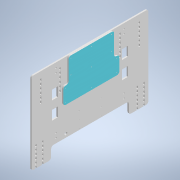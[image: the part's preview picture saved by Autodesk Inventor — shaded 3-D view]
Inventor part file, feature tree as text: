
AUTODESK INVENTOR PART (.ipt)
format: ipt  version: 2021.1 (Build 251245010, 245A)  size: 775,680 bytes
history: native  units: mm
features: reference x40, other x17, sketch x5, extrude x5, projected_geometry x1
ambient origin geometry x8: Origin, YZ Plane, XZ Plane, XY Plane, X Axis, Y Axis, Z Axis, Center Point
bodies: Body1 (feature_tree), Body2 (feature_tree)
feature tree (68):
  other  "Твердое тело1"
  other  "РабПлоскость1"
  sketch  "Эскиз1"
  other  "РабПлоскость2"
  extrude  "Выдавливание1"  Depth=350.0mm
  extrude  "Выдавливание2"  Depth=500.0mm
  extrude  "Выдавливание3"  Depth=59.22mm
  extrude  "Выдавливание4"  Depth=10.0mm
  extrude  "Выдавливание5"  Depth=10.0mm
  reference  "Ссылка13"
  reference  "Ссылка14"
  reference  "Ссылка15"
  reference  "Ссылка16"
  reference  "Ссылка17"
  reference  "Ссылка18"
  reference  "Ссылка19"
  reference  "Ссылка20"
  reference  "Ссылка21"
  reference  "Ссылка22"
  reference  "Ссылка23"
  reference  "Ссылка24"
  sketch  "Эскиз2"
  reference  "Ссылка53"
  reference  "Ссылка72"
  reference  "Ссылка75"
  reference  "Ссылка81"
  reference  "Ссылка82"
  reference  "Ссылка83"
  reference  "Ссылка84"
  reference  "Ссылка85"
  reference  "Ссылка86"
  reference  "Ссылка87"
  reference  "Ссылка88"
  sketch  "Эскиз3"
  reference  "Ссылка89"
  reference  "Ссылка90"
  reference  "Ссылка91"
  reference  "Ссылка92"
  reference  "Ссылка93"
  reference  "Ссылка94"
  sketch  "Эскиз5"
  other  "Твердое тело2"
  reference  "Ссылка95"
  reference  "Ссылка96"
  sketch  "Эскиз6"
  projected_geometry  "Спроецированная петля1"
  reference  "Ссылка97"
  reference  "Ссылка98"
  reference  "Ссылка99"
  reference  "Ссылка100"
  reference  "Ссылка101"
  reference  "Ссылка102"
  reference  "Ссылка103"
  reference  "Ссылка104"
  reference  "Ссылка105"
  parser-record x2  (decoder bookkeeping rows leaked as tree rows — omitted from the tree; the rows remain in map.json)
  other  "Mobile platform ispr.iam"
  other  "Krep i motor:2"
  other  "Krepleniye motor:1"
  other  "Sborka.iam"
  other  "Korpus:1"
  other  "корпус:1"
  other  "Krep i volokusha:1"
  other  "Volokusha:1"
  other  "44260_txm torquenado dc motor:1"
  other  "Krep i motor:1"
  other  "Сборка1"
note: 2 file-system paths scrubbed to <path> (originals preserved in map.json)
